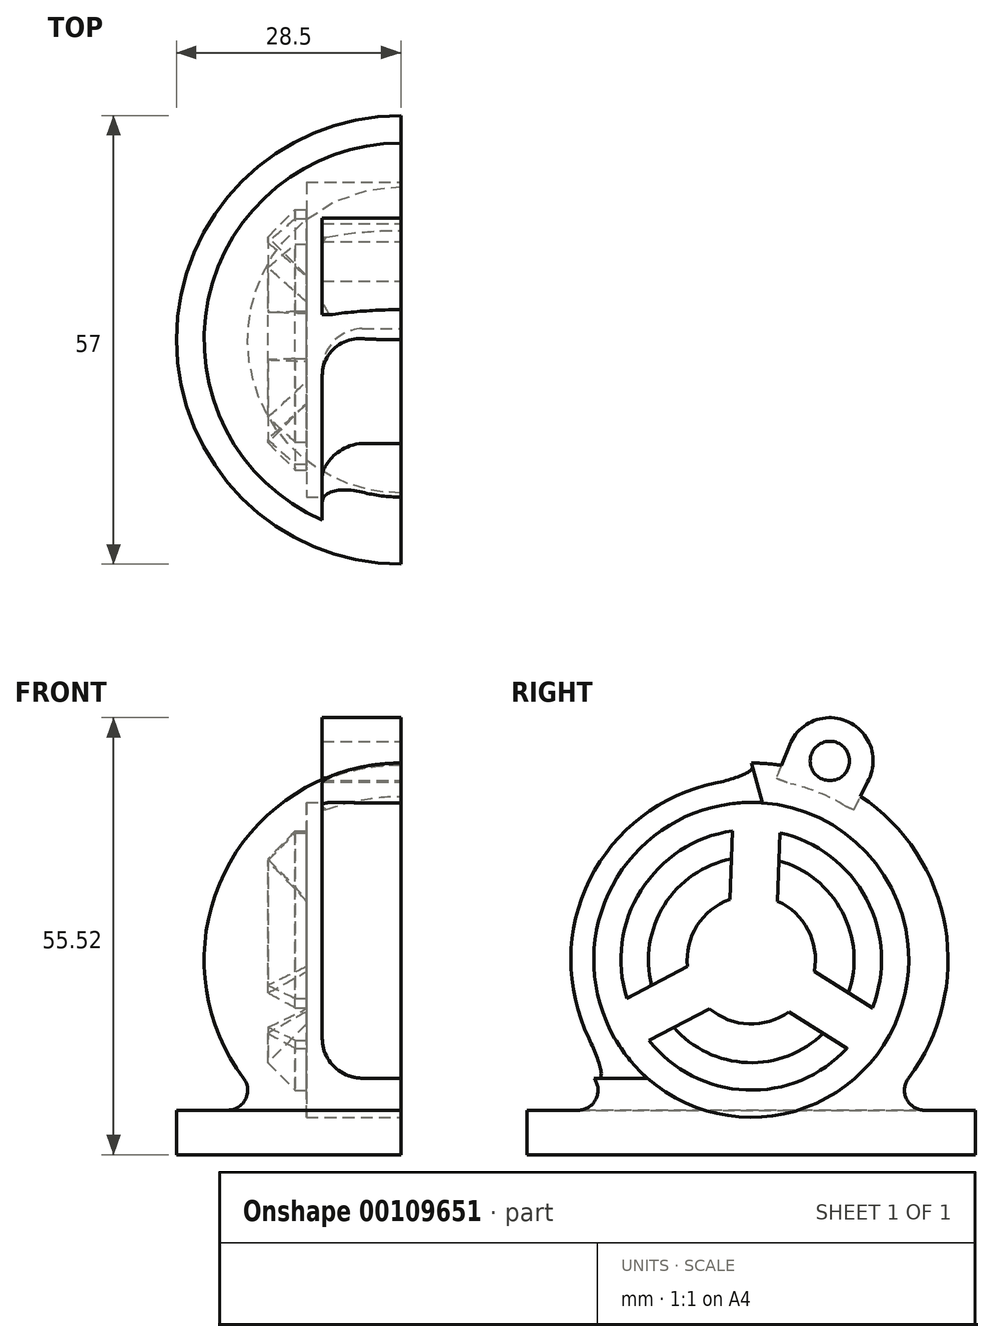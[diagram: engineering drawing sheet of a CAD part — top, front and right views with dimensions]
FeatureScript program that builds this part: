
annotation { "Feature Type Name" : "Feature", "Feature Type Description" : "" }
export const myFeature = defineFeature(function(context is Context, id is Id, definition is map)
    precondition{}
    {
        {
            var Q0;
            Q0=qCreatedBy(makeId("Right.planeOp"),FACE);
            var sketch = newSketch(context, id + "F0", { "sketchPlane" : qUnion([Q0])});
            skLineSegment(sketch, "E0", {"start": v(0, 0) * mm, "end": v(-28.5, 0) * mm});
            skLineSegment(sketch, "E1", {"start": v(-28.5, 0) * mm, "end": v(-28.5, 5.65) * mm});
            skLineSegment(sketch, "E2", {"start": v(-28.5, 5.65) * mm, "end": v(-16.13, 5.65) * mm});
            skArc(sketch, "E3.trimOffspring", {"start": v(0, 49.75) * mm, "mid": v(-23.48, 33.34) * mm, "end": v(-16.13, 5.65) * mm});
            skLineSegment(sketch, "E4", {"start": v(0, 49.75) * mm, "end": v(0, 0) * mm});
            skPoint(sketch, "E5.end.orphan", {"position": v(28.5, 0) * mm});
            skPoint(sketch, "E5.start.orphan", {"position": v(28.5, 5.65) * mm});
            skPoint(sketch, "E6.MirrorCS.start.orphan", {"position": v(0, 0) * mm});
            skSolve(sketch);
        }
        {
            var Q0;
            Q0=makeQuery(id+"F0.imprint","IMPRINT",FACE,{"disambiguationData":[TD([[makeQuery(id+"F0.imprint","IMPRINT",EDGE,{"derivedFrom":sQuery(id+"F0.wireOp",EDGE,"E0")}),-1.0]])]});
            var Q1;
            Q1=sQuery(id+"F0.wireOp",EDGE,"E4");
            revolve(context, id + "F1", {"entities" : qUnion([Q0]), "axis" : qUnion([Q1]), "revolveType" : RevolveType.ONE_DIRECTION, "angle" : 180 * degree});
        }
        {
            var Q0;
            Q0=makeQuery(id+"F1.opRevolve","SWEPT_EDGE",EDGE,{"disambiguationData":[OSD([sQuery(id+"F0.wireOp",EDGE,"E2"),sQuery(id+"F0.wireOp",EDGE,"E3.trimOffspring")])]});
            fillet(context, id + "F2", {"entities" : qUnion([Q0]), "radius" : 2.54 * mm, "tangentPropagation" : true, "allowEdgeOverflow" : false});
        }
        {
            var Q0;
            Q0=makeQuery(id+"F1.opRevolve","CAP_FACE",FACE,{"disambiguationData":[OSD([sQuery(id+"F0.wireOp",EDGE,"E0"),sQuery(id+"F0.wireOp",EDGE,"E1"),sQuery(id+"F0.wireOp",EDGE,"E2"),sQuery(id+"F0.wireOp",EDGE,"E3.trimOffspring"),sQuery(id+"F0.wireOp",EDGE,"E4")])],"isStart":false});
            var sketch = newSketch(context, id + "F3", { "sketchPlane" : qUnion([Q0])});
            skCircle(sketch, "E7", {"center": v(0, 24.75) * mm, "radius": 20 * mm});
            skSolve(sketch);
        }
        {
            var Q0;
            Q0 = qSketchRegion(id + "F3", true);
            extrude(context, id + "F4", {"entities" : qUnion([Q0]), "operationType" : NewBodyOperationType.REMOVE, "oppositeDirection" : true, "depth" : 12 * mm});
        }
        {
            var Q0;
            Q0=makeQuery(id+"F1.opRevolve","CAP_FACE",FACE,{"disambiguationData":[OSD([sQuery(id+"F0.wireOp",EDGE,"E0"),sQuery(id+"F0.wireOp",EDGE,"E1"),sQuery(id+"F0.wireOp",EDGE,"E2"),sQuery(id+"F0.wireOp",EDGE,"E3.trimOffspring"),sQuery(id+"F0.wireOp",EDGE,"E4")])],"isStart":false});
            var sketch = newSketch(context, id + "F5", { "sketchPlane" : qUnion([Q0])});
            skLineSegment(sketch, "E8", {"start": v(-19.98, 9.72) * mm, "end": v(-13.2, 9.72) * mm});
            skLineSegment(sketch, "E9", {"start": v(0, 49.75) * mm, "end": v(1.4, 44.7) * mm});
            skSolve(sketch);
        }
        {
            var Q0;
            {var subQ0=sQuery(id+"F5.wireOp",EDGE,"E8");Q0=makeQuery(id+"F5.imprint","IMPRINT",FACE,{"disambiguationData":[TD([[makeQuery(id+"F5.imprint","IMPRINT",EDGE,{"derivedFrom":subQ0}),1.0]])]});}
            extrude(context, id + "F6", {"entities" : qUnion([Q0]), "operationType" : NewBodyOperationType.REMOVE, "oppositeDirection" : true, "depth" : 10 * mm});
        }
        {
            var Q0;
            Q0=makeQuery(id+"F6.boolean.opBoolean","COPY",EDGE,{"derivedFrom":makeQuery(id+"F6.opExtrude","CAP_EDGE",EDGE,{"disambiguationData":[OSD([sQuery(id+"F5.wireOp",EDGE,"E8")])],"isStart":false})});
            var Q1;
            Q1=makeQuery(id+"F6.boolean.opBoolean","COPY",EDGE,{"derivedFrom":makeQuery(id+"F6.opExtrude","CAP_EDGE",EDGE,{"disambiguationData":[OSD([sQuery(id+"F5.wireOp",EDGE,"E9")])],"isStart":false})});
            fillet(context, id + "F7", {"entities" : qUnion([Q0, Q1]), "radius" : 5.08 * mm, "tangentPropagation" : true, "allowEdgeOverflow" : false});
        }
        {
            var Q0;
            Q0=makeQuery(id+"F4.boolean.opBoolean","COPY",FACE,{"derivedFrom":makeQuery(id+"F4.opExtrude","CAP_FACE",FACE,{"disambiguationData":[OSD([sQuery(id+"F3.wireOp",EDGE,"E7")])],"isStart":false})});
            var sketch = newSketch(context, id + "F8", { "sketchPlane" : qUnion([Q0])});
            skArc(sketch, "E10", {"start": v(-4.2, 19.11) * mm, "mid": v(-0.27, 17.72) * mm, "end": v(3.76, 18.8) * mm});
            skArc(sketch, "E11", {"start": v(-13, 14.5) * mm, "mid": v(-0.65, 8.2) * mm, "end": v(12.17, 13.52) * mm});
            skLineSegment(sketch, "E12", {"start": v(-4.2, 19.11) * mm, "end": v(-13, 14.5) * mm});
            skLineSegment(sketch, "E13", {"start": v(-15.81, 19.86) * mm, "end": v(-7.03, 24.46) * mm});
            skLineSegment(sketch, "E14", {"start": v(-2.78, 31.2) * mm, "end": v(-2.4, 41.13) * mm});
            skLineSegment(sketch, "E15", {"start": v(3.26, 30.98) * mm, "end": v(3.64, 40.9) * mm});
            skLineSegment(sketch, "E16", {"start": v(3.76, 18.8) * mm, "end": v(12.17, 13.52) * mm});
            skLineSegment(sketch, "E17", {"start": v(6.98, 23.93) * mm, "end": v(15.38, 18.64) * mm});
            skArc(sketch, "E18.trimOffspring", {"start": v(6.98, 23.93) * mm, "mid": v(6.22, 28.03) * mm, "end": v(3.26, 30.98) * mm});
            skArc(sketch, "E19.trimOffspring", {"start": v(15.38, 18.64) * mm, "mid": v(14.64, 32.48) * mm, "end": v(3.64, 40.9) * mm});
            skArc(sketch, "E20.trimOffspring", {"start": v(-2.4, 41.13) * mm, "mid": v(-14, 33.58) * mm, "end": v(-15.81, 19.86) * mm});
            skArc(sketch, "E21.trimOffspring", {"start": v(-2.78, 31.2) * mm, "mid": v(-5.95, 28.5) * mm, "end": v(-7.03, 24.46) * mm});
            skSolve(sketch);
        }
        {
            var Q0;
            Q0=makeQuery(id+"F8.imprint","IMPRINT",FACE,{"disambiguationData":[TD([[makeQuery(id+"F8.imprint","IMPRINT",EDGE,{"derivedFrom":sQuery(id+"F8.wireOp",EDGE,"E15")}),-1.0]])]});
            var Q1;
            Q1=makeQuery(id+"F8.imprint","IMPRINT",FACE,{"disambiguationData":[TD([[makeQuery(id+"F8.imprint","IMPRINT",EDGE,{"derivedFrom":sQuery(id+"F8.wireOp",EDGE,"E13")}),1.0]])]});
            var Q2;
            Q2=makeQuery(id+"F8.imprint","IMPRINT",FACE,{"disambiguationData":[TD([[makeQuery(id+"F8.imprint","IMPRINT",EDGE,{"derivedFrom":sQuery(id+"F8.wireOp",EDGE,"E10")}),-1.0]])]});
            extrude(context, id + "F9", {"entities" : qUnion([Q0, Q1, Q2]), "operationType" : NewBodyOperationType.REMOVE, "oppositeDirection" : true, "depth" : 6.5 * mm});
        }
        {
            var Q0;
            Q0=makeQuery(id+"F9.boolean.opBoolean","COPY",EDGE,{"derivedFrom":makeQuery(id+"F9.opExtrude","CAP_EDGE",EDGE,{"disambiguationData":[OSD([sQuery(id+"F8.wireOp",EDGE,"E19.trimOffspring")])],"isStart":false})});
            var Q1;
            Q1=makeQuery(id+"F9.boolean.opBoolean","COPY",EDGE,{"derivedFrom":makeQuery(id+"F9.opExtrude","CAP_EDGE",EDGE,{"disambiguationData":[OSD([sQuery(id+"F8.wireOp",EDGE,"E20.trimOffspring")])],"isStart":false})});
            var Q2;
            Q2=makeQuery(id+"F9.boolean.opBoolean","COPY",EDGE,{"derivedFrom":makeQuery(id+"F9.opExtrude","CAP_EDGE",EDGE,{"disambiguationData":[OSD([sQuery(id+"F8.wireOp",EDGE,"E11")])],"isStart":false})});
            chamfer(context, id + "F10", {"entities" : qUnion([Q0, Q1, Q2]), "width" : 5.08 * mm, "tangentPropagation" : true});
        }
        {
            var Q0;
            Q0=makeQuery(id+"F9.boolean.opBoolean","COPY",EDGE,{"derivedFrom":makeQuery(id+"F9.opExtrude","CAP_EDGE",EDGE,{"disambiguationData":[OSD([sQuery(id+"F8.wireOp",EDGE,"E21.trimOffspring")])],"isStart":false})});
            var Q1;
            Q1=makeQuery(id+"F9.boolean.opBoolean","COPY",EDGE,{"derivedFrom":makeQuery(id+"F9.opExtrude","CAP_EDGE",EDGE,{"disambiguationData":[OSD([sQuery(id+"F8.wireOp",EDGE,"E18.trimOffspring")])],"isStart":false})});
            var Q2;
            Q2=makeQuery(id+"F9.boolean.opBoolean","COPY",EDGE,{"derivedFrom":makeQuery(id+"F9.opExtrude","CAP_EDGE",EDGE,{"disambiguationData":[OSD([sQuery(id+"F8.wireOp",EDGE,"E10")])],"isStart":false})});
            chamfer(context, id + "F11", {"entities" : qUnion([Q0, Q1, Q2]), "width" : 7.62 * mm, "tangentPropagation" : true});
        }
        {
            var Q0;
            Q0=qCreatedBy(makeId("Right.planeOp"),FACE);
            var sketch = newSketch(context, id + "F12", { "sketchPlane" : qUnion([Q0])});
            skArc(sketch, "E22", {"start": v(14.78, 47.32) * mm, "mid": v(12.37, 54.97) * mm, "end": v(4.89, 52.08) * mm});
            skLineSegment(sketch, "E23", {"start": v(4.89, 52.08) * mm, "end": v(3.17, 47.84) * mm});
            skLineSegment(sketch, "E24", {"start": v(3.17, 47.84) * mm, "end": v(13.06, 43.84) * mm});
            skLineSegment(sketch, "E25", {"start": v(13.06, 43.84) * mm, "end": v(14.78, 47.32) * mm});
            skSolve(sketch);
        }
        {
            var Q0;
            Q0 = qSketchRegion(id + "F12", true);
            extrude(context, id + "F13", {"entities" : qUnion([Q0]), "operationType" : NewBodyOperationType.ADD, "oppositeDirection" : true, "depth" : 10 * mm});
        }
        {
            var Q0;
            Q0=makeQuery(id+"F13.boolean.opBoolean","MERGE",FACE,{"derivedFrom":[makeQuery(id+"F1.opRevolve","CAP_FACE",FACE,{"disambiguationData":[OSD([sQuery(id+"F0.wireOp",EDGE,"E0"),sQuery(id+"F0.wireOp",EDGE,"E1"),sQuery(id+"F0.wireOp",EDGE,"E2"),sQuery(id+"F0.wireOp",EDGE,"E3.trimOffspring"),sQuery(id+"F0.wireOp",EDGE,"E4")])],"isStart":false}),makeQuery(id+"F13.opExtrude","CAP_FACE",FACE,{"disambiguationData":[OSD([sQuery(id+"F12.wireOp",EDGE,"E22"),sQuery(id+"F12.wireOp",EDGE,"E23"),sQuery(id+"F12.wireOp",EDGE,"E24"),sQuery(id+"F12.wireOp",EDGE,"E25")])],"isStart":true})]});
            var sketch = newSketch(context, id + "F14", { "sketchPlane" : qUnion([Q0])});
            skCircle(sketch, "E26", {"center": v(9.98, 50.02) * mm, "radius": 2.5 * mm});
            skSolve(sketch);
        }
        {
            var Q0;
            Q0 = qSketchRegion(id + "F14", true);
            extrude(context, id + "F15", {"entities" : qUnion([Q0]), "operationType" : NewBodyOperationType.REMOVE, "endBound" : BoundingType.THROUGH_ALL, "oppositeDirection" : true, "depth" : 25.4 * mm});
        }
    });
